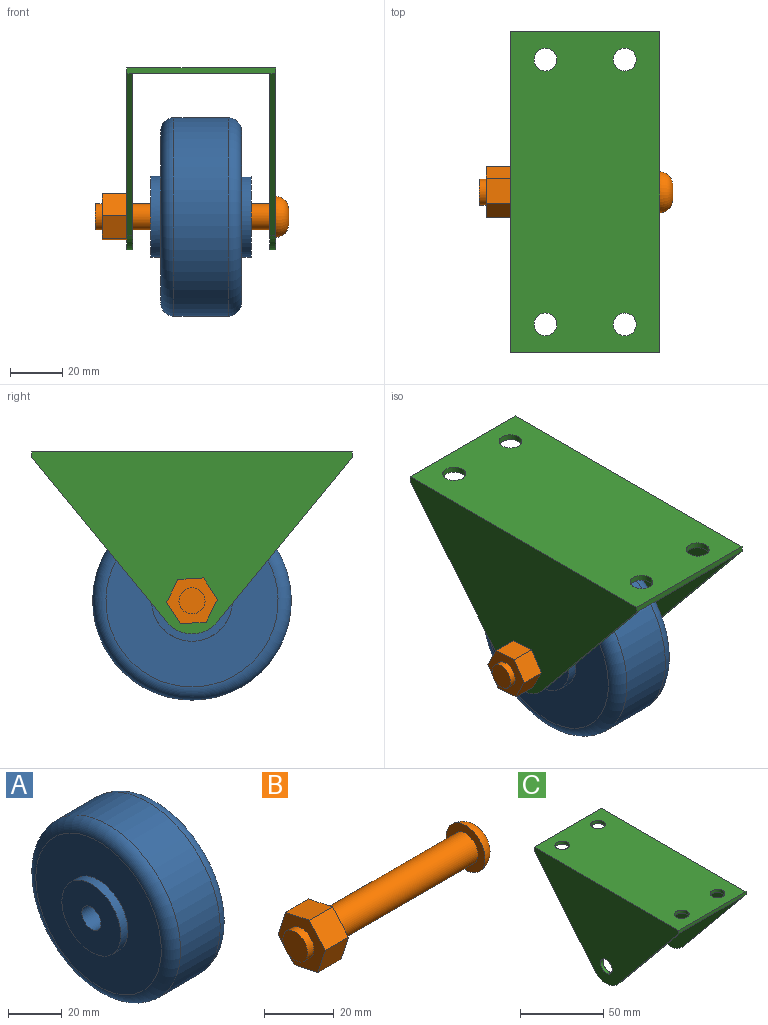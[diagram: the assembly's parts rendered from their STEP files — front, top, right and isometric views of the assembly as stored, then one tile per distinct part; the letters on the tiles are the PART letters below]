
ASSEMBLY  parts=3 mates=4
PART A: 10 faces, bbox 38.6x82.5x82.5 mm
  f0: cylinder r=38.1mm len=76.2mm, axis (-1,0,0), area 4988.9mm2, adj f3,f4
  f1: plane 66.04x66.04mm, normal (1,0,0), area 2670.6mm2, adj f4,f5
  f2: plane 66.04x66.04mm, normal (-1,0,0), area 2670.6mm2, adj f3,f7
  f3: torus R=33.02mm, axis (1,0,0), area 1817.7mm2, adj f0,f2
  f4: torus R=33.02mm, axis (1,0,0), area 1817.7mm2, adj f0,f1
  f5: cylinder r=15.5mm len=31mm, axis (-1,0,0), area 371.1mm2, adj f1,f6
  f6: plane 31x31mm, normal (1,0,0), area 676.2mm2, adj f5,f9
  f7: cylinder r=15.5mm len=31mm, axis (1,0,0), area 371.1mm2, adj f2,f8
  f8: plane 31x31mm, normal (-1,0,0), area 676.2mm2, adj f7,f9
  f9: cylinder r=5mm len=38.62mm, axis (1,0,0), area 1213.3mm2, adj f6,f8
PART B: 14 faces, bbox 74.2x19.2x18.7 mm
  f0: cylinder r=5mm len=57.15mm, axis (1,0,0), area 1795.4mm2, adj f2,f11
  f1: plane 5.54x5.54mm, normal (1,0,0), area 24.1mm2, adj f3
  f2: plane 15.7x15.7mm, normal (-1,0,0), area 115.1mm2, adj f0,f3
  f3: torus R=2.77mm, axis (-1,0,0), area 297.1mm2, adj f1,f2
  f4: plane 9.4x7.31mm, normal (0,0.75,-0.67), area 92.3mm2, adj f5,f9,f10,f11
  f5: plane 9.61x9.4mm, normal (0,-0.21,-0.98), area 92.3mm2, adj f4,f6,f10,f11
  f6: plane 9.4x9.33mm, normal (0,-0.95,-0.31), area 92.3mm2, adj f5,f7,f10,f11
  f7: plane 9.4x7.31mm, normal (0,-0.75,0.67), area 92.3mm2, adj f6,f8,f10,f11
  f8: plane 9.61x9.4mm, normal (0,0.21,0.98), area 92.3mm2, adj f7,f9,f10,f11
  f9: plane 9.4x9.33mm, normal (0,0.95,0.31), area 92.3mm2, adj f4,f8,f10,f11
  f10: plane 19.21x18.65mm, normal (-1,0,0), area 171.7mm2, adj f4,f5,f6,f7,f8,f9,f13
  f11: plane 19.21x18.65mm, normal (1,0,0), area 171.7mm2, adj f0,f4,f5,f6,f7,f8,f9
  f12: plane 10x10mm, normal (-1,0,0), area 78.5mm2, adj f13
  f13: cylinder r=5mm len=10mm, axis (1,0,0), area 81.7mm2, adj f10,f12
PART C: 20 faces, bbox 57.2x123x69.9 mm
  f0: plane 123x52.58mm, normal (0,0,-1), area 6225.9mm2, adj f1,f3,f10,f15,f16,f17,f18,f19
  f1: plane 57.15x2.29mm, normal (0,-1,0), area 130.6mm2, adj f0,f2,f4,f5,f7,f12
  f2: plane 123x69.85mm, normal (1,0,0), area 4750.5mm2, adj f1,f3,f5,f6,f7,f8,f9
  f3: plane 57.15x2.29mm, normal (0,1,0), area 130.6mm2, adj f0,f2,f4,f5,f6,f11
  f4: plane 123x69.85mm, normal (-1,0,0), area 4750.5mm2, adj f1,f3,f5,f11,f12,f13,f14
  f5: plane 123x57.15mm, normal (0,0,1), area 6788.2mm2, adj f1,f2,f3,f4,f16,f17,f18,f19
  f6: plane 62.17x51.11mm, normal (0,0.77,-0.64), area 184mm2, adj f2,f3,f8,f10
  f7: plane 62.17x51.11mm, normal (0,-0.77,-0.64), area 184mm2, adj f1,f2,f8,f10
  f8: cylinder r=12.7mm len=20.78mm, axis (1,0,0), area 55.6mm2, adj f2,f6,f7,f10
  f9: cylinder r=5mm len=10mm, axis (1,0,0), area 71.8mm2, adj f2,f10
  f10: plane 123x67.56mm, normal (-1,0,0), area 4469.3mm2, adj f0,f6,f7,f8,f9
  f11: plane 62.17x51.11mm, normal (0,0.77,-0.64), area 184mm2, adj f3,f4,f13,f15
  f12: plane 62.17x51.11mm, normal (0,-0.77,-0.64), area 184mm2, adj f1,f4,f13,f15
  f13: cylinder r=12.7mm len=20.78mm, axis (-1,0,0), area 55.6mm2, adj f4,f11,f12,f15
  f14: cylinder r=5mm len=10mm, axis (-1,0,0), area 71.8mm2, adj f4,f15
  f15: plane 123x67.56mm, normal (1,0,0), area 4469.3mm2, adj f0,f11,f12,f13,f14
  f16: cylinder r=4.38mm len=8.76mm, axis (0,0,1), area 62.9mm2, adj f0,f5
  f17: cylinder r=4.38mm len=8.76mm, axis (0,0,1), area 62.9mm2, adj f0,f5
  f18: cylinder r=4.38mm len=8.76mm, axis (0,0,1), area 62.9mm2, adj f0,f5
  f19: cylinder r=4.38mm len=8.76mm, axis (0,0,1), area 62.9mm2, adj f0,f5
PLACE A t=(-47.11,-51.18,19.26)mm fixed
PLACE B rot(axis=(1,0,0),8.3deg) t=(-47.11,-59.09,73.55)mm
PLACE C rot(axis=(-1,0,0),0deg) t=(-47.11,-51.18,74.12)mm
MATE planar C.f10 <-> A.f0  axis (-1,0,0) through (-20.82,-87.12,43.04)mm
MATE cylindrical A.f9 <-> B.f0  axis (1,0,0) through (-27.8,-51.18,19.26)mm
MATE planar C.f2 <-> B.f0  axis (1,0,0) through (-18.53,-51.18,51.72)mm
MATE cylindrical B.f0 <-> C.f9  axis (1,0,0) through (-18.53,-51.18,19.26)mm
